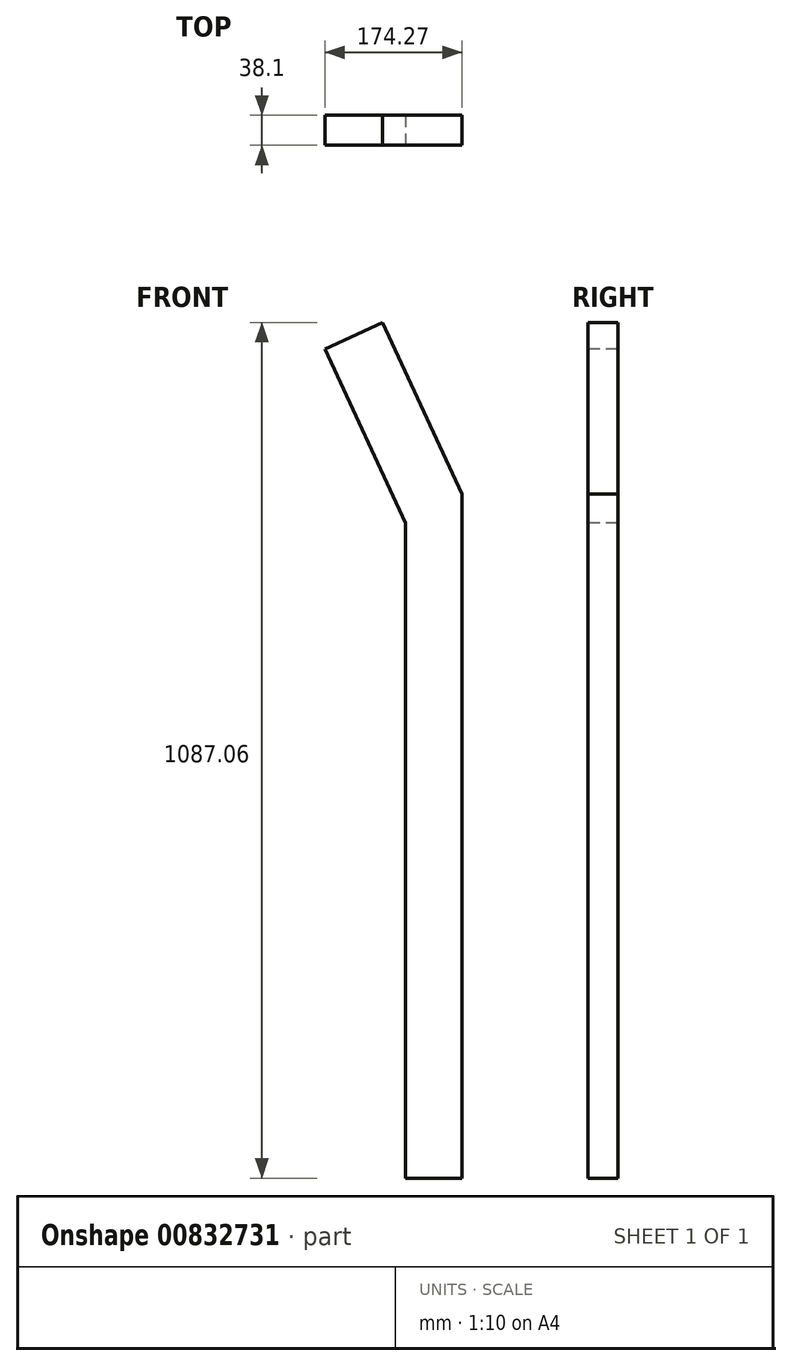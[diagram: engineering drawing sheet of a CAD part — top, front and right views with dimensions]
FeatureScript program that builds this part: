
annotation { "Feature Type Name" : "Feature", "Feature Type Description" : "" }
export const myFeature = defineFeature(function(context is Context, id is Id, definition is map)
    precondition{}
    {
        {
            var Q0;
            Q0=qCreatedBy(makeId("Front.planeOp"),FACE);
            var sketch = newSketch(context, id + "F0", { "sketchPlane" : qUnion([Q0])});
            skLineSegment(sketch, "E0.bottom", {"start": v(0, 0) * mm, "end": v(190.5, 0) * mm});
            skLineSegment(sketch, "E0.top", {"start": v(0, 1219.2) * mm, "end": v(190.5, 1219.2) * mm});
            skLineSegment(sketch, "E0.left", {"start": v(0, 0) * mm, "end": v(0, 1219.2) * mm});
            skLineSegment(sketch, "E0.right", {"start": v(190.5, 0) * mm, "end": v(190.5, 1219.2) * mm});
            skLineSegment(sketch, "E1", {"start": v(118.67, 0) * mm, "end": v(118.67, 832.27) * mm});
            skLineSegment(sketch, "E2", {"start": v(118.67, 832.27) * mm, "end": v(16.23, 1053.14) * mm});
            skLineSegment(sketch, "E3", {"start": v(16.23, 1053.14) * mm, "end": v(89.37, 1087.06) * mm});
            skLineSegment(sketch, "E4", {"start": v(89.37, 1087.06) * mm, "end": v(190.5, 869) * mm});
            skSolve(sketch);
        }
        {
            var Q0;
            Q0=makeQuery(id+"F0.imprint","IMPRINT",FACE,{"disambiguationData":[TD([[makeQuery(id+"F0.imprint","IMPRINT",EDGE,{"derivedFrom":sQuery(id+"F0.wireOp",EDGE,"E0.bottom")}),1.0]])]});
            extrude(context, id + "F1", {"entities" : qUnion([Q0]), "oppositeDirection" : true, "depth" : 38.1 * mm, "offsetDistance" : 25.4 * mm});
        }
    });
